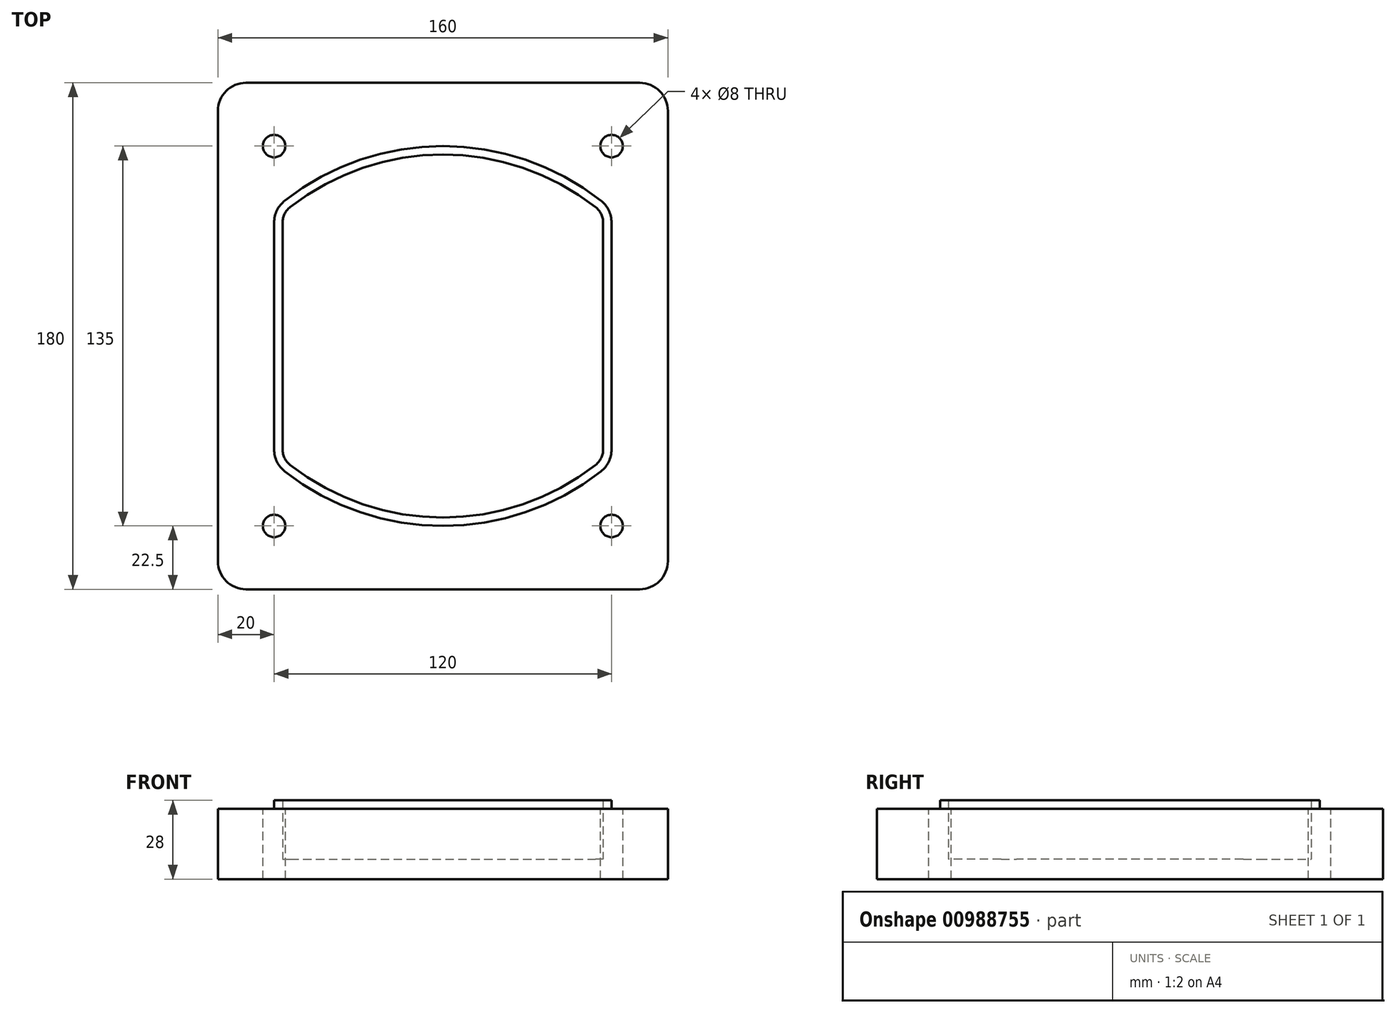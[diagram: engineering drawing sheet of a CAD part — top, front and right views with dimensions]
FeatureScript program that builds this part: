
annotation { "Feature Type Name" : "Feature", "Feature Type Description" : "" }
export const myFeature = defineFeature(function(context is Context, id is Id, definition is map)
    precondition{}
    {
        {
            var Q0;
            Q0=qCreatedBy(makeId("Top.planeOp"),FACE);
            var sketch = newSketch(context, id + "F0", { "sketchPlane" : qUnion([Q0])});
            skPoint(sketch, "E0.rect.middle", {"position": v(0, 0) * mm});
            skLineSegment(sketch, "E1.bottom", {"start": v(-70, -90) * mm, "end": v(70, -90) * mm});
            skLineSegment(sketch, "E1.top", {"start": v(-70, 90) * mm, "end": v(70, 90) * mm});
            skLineSegment(sketch, "E1.left", {"start": v(-80, -80) * mm, "end": v(-80, 80) * mm});
            skLineSegment(sketch, "E1.right", {"start": v(80, -80) * mm, "end": v(80, 80) * mm});
            skLineSegment(sketch, "E2", {"start": v(-80, 90) * mm, "end": v(80, -90) * mm, "construction": true});
            skLineSegment(sketch, "E3", {"start": v(80, 90) * mm, "end": v(-80, -90) * mm, "construction": true});
            skCircle(sketch, "E4", {"center": v(-60, 67.5) * mm, "radius": 4 * mm});
            skCircle(sketch, "E5", {"center": v(60, 67.5) * mm, "radius": 4 * mm});
            skCircle(sketch, "E6", {"center": v(60, -67.5) * mm, "radius": 4 * mm});
            skCircle(sketch, "E7", {"center": v(-60, -67.5) * mm, "radius": 4 * mm});
            skLineSegment(sketch, "E8", {"start": v(-60, 67.5) * mm, "end": v(60, 67.5) * mm, "construction": true});
            skLineSegment(sketch, "E9", {"start": v(60, 67.5) * mm, "end": v(60, -67.5) * mm, "construction": true});
            skLineSegment(sketch, "E10", {"start": v(60, -67.5) * mm, "end": v(-60, -67.5) * mm, "construction": true});
            skLineSegment(sketch, "E11", {"start": v(-60, -67.5) * mm, "end": v(-60, 67.5) * mm, "construction": true});
            skLineSegment(sketch, "E12", {"start": v(-60, 40.3) * mm, "end": v(-60, -40.3) * mm});
            skLineSegment(sketch, "E13", {"start": v(60, 40.3) * mm, "end": v(60, -40.3) * mm});
            skArc(sketch, "E14", {"start": v(56.15, 48.18) * mm, "mid": v(0, 67.5) * mm, "end": v(-56.15, 48.18) * mm});
            skArc(sketch, "E15", {"start": v(-56.15, -48.18) * mm, "mid": v(0, -67.5) * mm, "end": v(56.15, -48.18) * mm});
            skLineSegment(sketch, "E16", {"start": v(-60, 0) * mm, "end": v(60, 0) * mm, "construction": true});
            skPoint(sketch, "E17.visualSharp", {"position": v(-60, -45) * mm});
            skArc(sketch, "E17.filletArc", {"start": v(-60, -40.3) * mm, "mid": v(-58.99, -44.68) * mm, "end": v(-56.15, -48.18) * mm});
            skPoint(sketch, "E18.visualSharp", {"position": v(-60, 45) * mm});
            skArc(sketch, "E18.filletArc", {"start": v(-56.15, 48.18) * mm, "mid": v(-58.99, 44.68) * mm, "end": v(-60, 40.3) * mm});
            skPoint(sketch, "E19.visualSharp", {"position": v(60, 45) * mm});
            skArc(sketch, "E19.filletArc", {"start": v(60, 40.3) * mm, "mid": v(58.99, 44.68) * mm, "end": v(56.15, 48.18) * mm});
            skPoint(sketch, "E20.visualSharp", {"position": v(60, -45) * mm});
            skArc(sketch, "E20.filletArc", {"start": v(56.15, -48.18) * mm, "mid": v(58.99, -44.68) * mm, "end": v(60, -40.3) * mm});
            skPoint(sketch, "E21.visualSharp", {"position": v(-80, 90) * mm});
            skArc(sketch, "E21.filletArc", {"start": v(-70, 90) * mm, "mid": v(-77.07, 87.07) * mm, "end": v(-80, 80) * mm});
            skPoint(sketch, "E22.visualSharp", {"position": v(80, 90) * mm});
            skArc(sketch, "E22.filletArc", {"start": v(80, 80) * mm, "mid": v(77.07, 87.07) * mm, "end": v(70, 90) * mm});
            skPoint(sketch, "E23.visualSharp", {"position": v(80, -90) * mm});
            skArc(sketch, "E23.filletArc", {"start": v(70, -90) * mm, "mid": v(77.07, -87.07) * mm, "end": v(80, -80) * mm});
            skPoint(sketch, "E24.visualSharp", {"position": v(-80, -90) * mm});
            skArc(sketch, "E24.filletArc", {"start": v(-80, -80) * mm, "mid": v(-77.07, -87.07) * mm, "end": v(-70, -90) * mm});
            skArc(sketch, "E25.0", {"start": v(57, 40.3) * mm, "mid": v(56.3, 43.36) * mm, "end": v(54.3, 45.81) * mm});
            skLineSegment(sketch, "E25.1", {"start": v(57, 40.3) * mm, "end": v(57, -40.3) * mm});
            skArc(sketch, "E25.2", {"start": v(54.3, -45.81) * mm, "mid": v(56.3, -43.36) * mm, "end": v(57, -40.3) * mm});
            skArc(sketch, "E25.3", {"start": v(-54.3, -45.81) * mm, "mid": v(0, -64.5) * mm, "end": v(54.3, -45.81) * mm});
            skArc(sketch, "E25.4", {"start": v(-57, -40.3) * mm, "mid": v(-56.3, -43.36) * mm, "end": v(-54.3, -45.81) * mm});
            skArc(sketch, "E25.5", {"start": v(54.3, 45.81) * mm, "mid": v(0, 64.5) * mm, "end": v(-54.3, 45.81) * mm});
            skLineSegment(sketch, "E25.6", {"start": v(-57, 40.3) * mm, "end": v(-57, -40.3) * mm});
            skArc(sketch, "E25.7", {"start": v(-54.3, 45.81) * mm, "mid": v(-56.3, 43.36) * mm, "end": v(-57, 40.3) * mm});
            skArc(sketch, "E26.0", {"start": v(-58.62, 51.33) * mm, "mid": v(-62.58, 46.43) * mm, "end": v(-64, 40.3) * mm});
            skArc(sketch, "E26.1", {"start": v(58.62, 51.33) * mm, "mid": v(0, 71.5) * mm, "end": v(-58.62, 51.33) * mm});
            skArc(sketch, "E26.2", {"start": v(64, 40.3) * mm, "mid": v(62.58, 46.43) * mm, "end": v(58.62, 51.33) * mm});
            skLineSegment(sketch, "E26.3", {"start": v(64, 40.3) * mm, "end": v(64, -40.3) * mm});
            skArc(sketch, "E26.4", {"start": v(58.62, -51.33) * mm, "mid": v(62.58, -46.43) * mm, "end": v(64, -40.3) * mm});
            skLineSegment(sketch, "E26.5", {"start": v(-64, 40.3) * mm, "end": v(-64, -40.3) * mm});
            skArc(sketch, "E26.6", {"start": v(-58.62, -51.33) * mm, "mid": v(0, -71.5) * mm, "end": v(58.62, -51.33) * mm});
            skArc(sketch, "E26.7", {"start": v(-64, -40.3) * mm, "mid": v(-62.58, -46.43) * mm, "end": v(-58.62, -51.33) * mm});
            skSolve(sketch);
        }
        {
            var Q0;
            Q0=makeQuery(id+"F0.imprint","IMPRINT",FACE,{"disambiguationData":[TD([[makeQuery(id+"F0.imprint","IMPRINT",EDGE,{"derivedFrom":sQuery(id+"F0.wireOp",EDGE,"E1.bottom")}),1.0]])]});
            var Q1;
            Q1=makeQuery(id+"F0.imprint","IMPRINT",FACE,{"disambiguationData":[TD([[makeQuery(id+"F0.imprint","IMPRINT",EDGE,{"derivedFrom":sQuery(id+"F0.wireOp",EDGE,"E12")}),1.0]])]});
            var Q2;
            Q2=makeQuery(id+"F0.imprint","IMPRINT",FACE,{"disambiguationData":[TD([[makeQuery(id+"F0.imprint","IMPRINT",EDGE,{"derivedFrom":sQuery(id+"F0.wireOp",EDGE,"E25.0")}),1.0]])]});
            var Q3;
            Q3=makeQuery(id+"F0.imprint","IMPRINT",FACE,{"disambiguationData":[TD([[makeQuery(id+"F0.imprint","IMPRINT",EDGE,{"derivedFrom":sQuery(id+"F0.wireOp",EDGE,"E12")}),-1.0]])]});
            extrude(context, id + "F1", {"entities" : qUnion([Q0, Q1, Q2, Q3]), "oppositeDirection" : true, "depth" : 25 * mm});
        }
        {
            var Q0;
            Q0=makeQuery(id+"F0.imprint","IMPRINT",FACE,{"disambiguationData":[TD([[makeQuery(id+"F0.imprint","IMPRINT",EDGE,{"derivedFrom":sQuery(id+"F0.wireOp",EDGE,"E12")}),1.0]])]});
            extrude(context, id + "F2", {"entities" : qUnion([Q0]), "operationType" : NewBodyOperationType.ADD, "depth" : 3 * mm});
        }
        {
            var Q0;
            Q0=makeQuery(id+"F0.imprint","IMPRINT",FACE,{"disambiguationData":[TD([[makeQuery(id+"F0.imprint","IMPRINT",EDGE,{"derivedFrom":sQuery(id+"F0.wireOp",EDGE,"E25.0")}),1.0]])]});
            extrude(context, id + "F3", {"entities" : qUnion([Q0]), "operationType" : NewBodyOperationType.REMOVE, "oppositeDirection" : true, "depth" : 18 * mm});
        }
    });
